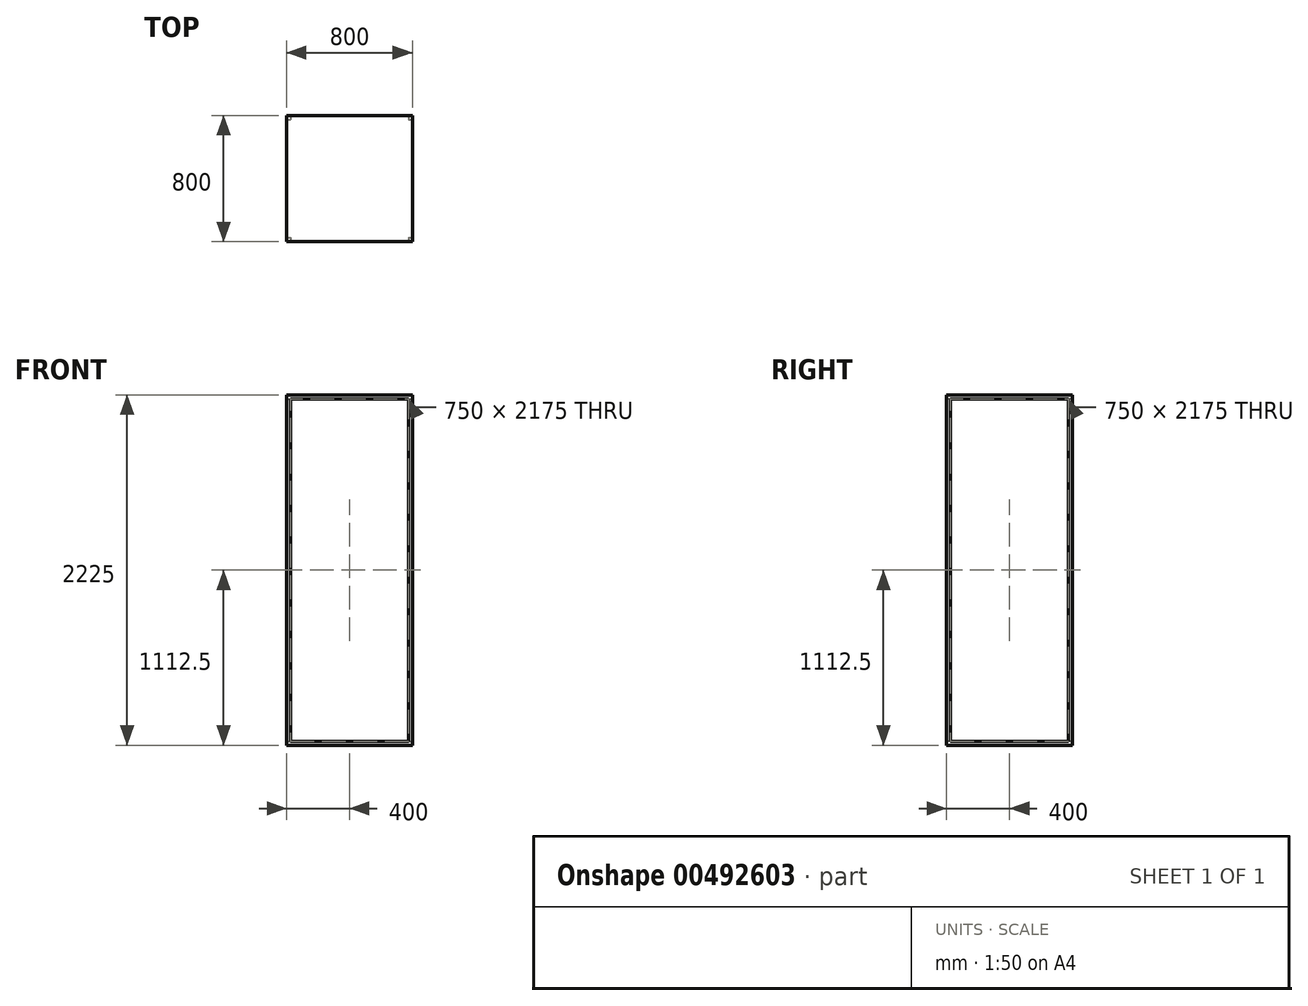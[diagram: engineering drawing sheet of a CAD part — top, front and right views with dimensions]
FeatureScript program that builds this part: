
annotation { "Feature Type Name" : "Feature", "Feature Type Description" : "" }
export const myFeature = defineFeature(function(context is Context, id is Id, definition is map)
    precondition{}
    {
        {
            var Q0;
            Q0=qCreatedBy(makeId("Front.planeOp"),FACE);
            var sketch = newSketch(context, id + "F0", { "sketchPlane" : qUnion([Q0])});
            skLineSegment(sketch, "E0.bottom", {"start": v(400, 1112.5) * mm, "end": v(-400, 1112.5) * mm});
            skLineSegment(sketch, "E0.top", {"start": v(400, -1112.5) * mm, "end": v(-400, -1112.5) * mm});
            skLineSegment(sketch, "E0.left", {"start": v(400, 1112.5) * mm, "end": v(400, -1112.5) * mm});
            skLineSegment(sketch, "E0.right", {"start": v(-400, 1112.5) * mm, "end": v(-400, -1112.5) * mm});
            skPoint(sketch, "E0.middle", {"position": v(0, 0) * mm});
            skSolve(sketch);
        }
        {
            var Q0;
            Q0=makeQuery(id+"F0.imprint","IMPRINT",FACE,{"disambiguationData":[TD([[makeQuery(id+"F0.imprint","IMPRINT",EDGE,{"derivedFrom":sQuery(id+"F0.wireOp",EDGE,"E0.bottom")}),1.0]])]});
            extrude(context, id + "F1", {"entities" : qUnion([Q0]), "depth" : 800 * mm});
        }
        {
            var Q0;
            Q0=makeQuery(id+"F1.opExtrude","CAP_FACE",FACE,{"disambiguationData":[OSD([sQuery(id+"F0.wireOp",EDGE,"E0.bottom"),sQuery(id+"F0.wireOp",EDGE,"E0.top"),sQuery(id+"F0.wireOp",EDGE,"E0.left"),sQuery(id+"F0.wireOp",EDGE,"E0.right")])],"isStart":false});
            var sketch = newSketch(context, id + "F2", { "sketchPlane" : qUnion([Q0])});
            skLineSegment(sketch, "E1.bottom", {"start": v(375, 1087.5) * mm, "end": v(-375, 1087.5) * mm});
            skLineSegment(sketch, "E1.top", {"start": v(375, -1087.5) * mm, "end": v(-375, -1087.5) * mm});
            skLineSegment(sketch, "E1.left", {"start": v(375, 1087.5) * mm, "end": v(375, -1087.5) * mm});
            skLineSegment(sketch, "E1.right", {"start": v(-375, 1087.5) * mm, "end": v(-375, -1087.5) * mm});
            skPoint(sketch, "E1.middle", {"position": v(0, 0) * mm});
            skSolve(sketch);
        }
        {
            var Q0;
            Q0=makeQuery(id+"F2.imprint","IMPRINT",FACE,{"disambiguationData":[TD([[makeQuery(id+"F2.imprint","IMPRINT",EDGE,{"derivedFrom":sQuery(id+"F2.wireOp",EDGE,"E1.bottom")}),1.0]])]});
            var Q1;
            Q1=makeQuery(id+"F1.opExtrude","CAP_FACE",FACE,{"disambiguationData":[OSD([sQuery(id+"F0.wireOp",EDGE,"E0.bottom"),sQuery(id+"F0.wireOp",EDGE,"E0.top"),sQuery(id+"F0.wireOp",EDGE,"E0.left"),sQuery(id+"F0.wireOp",EDGE,"E0.right")])],"isStart":true});
            extrude(context, id + "F3", {"entities" : qUnion([Q0]), "operationType" : NewBodyOperationType.REMOVE, "endBound" : BoundingType.UP_TO_SURFACE, "oppositeDirection" : true, "endBoundEntityFace" : qUnion([Q1]), "depth" : 25 * mm});
        }
        {
            var Q0;
            Q0=makeQuery(id+"F1.opExtrude","SWEPT_FACE",FACE,{"disambiguationData":[OSD([sQuery(id+"F0.wireOp",EDGE,"E0.left")])]});
            var sketch = newSketch(context, id + "F4", { "sketchPlane" : qUnion([Q0])});
            skLineSegment(sketch, "E2.bottom", {"start": v(-25, 1087.5) * mm, "end": v(-775, 1087.5) * mm});
            skLineSegment(sketch, "E2.top", {"start": v(-25, -1087.5) * mm, "end": v(-775, -1087.5) * mm});
            skLineSegment(sketch, "E2.left", {"start": v(-25, 1087.5) * mm, "end": v(-25, -1087.5) * mm});
            skLineSegment(sketch, "E2.right", {"start": v(-775, 1087.5) * mm, "end": v(-775, -1087.5) * mm});
            skPoint(sketch, "E2.middle", {"position": v(-400, 0) * mm});
            skPoint(sketch, "E2.middle.positionSnap0", {"position": v(-400, 1112.5) * mm});
            skPoint(sketch, "E2.centerSnap0", {"position": v(-400, 1112.5) * mm});
            skSolve(sketch);
        }
        {
            var Q0;
            Q0=makeQuery(id+"F4.imprint","IMPRINT",FACE,{"disambiguationData":[TD([[makeQuery(id+"F4.imprint","IMPRINT",EDGE,{"derivedFrom":sQuery(id+"F4.wireOp",EDGE,"E2.bottom")}),1.0]])]});
            var Q1;
            Q1=makeQuery(id+"F1.opExtrude","SWEPT_FACE",FACE,{"disambiguationData":[OSD([sQuery(id+"F0.wireOp",EDGE,"E0.right")])]});
            extrude(context, id + "F5", {"entities" : qUnion([Q0]), "operationType" : NewBodyOperationType.REMOVE, "endBound" : BoundingType.UP_TO_SURFACE, "oppositeDirection" : true, "endBoundEntityFace" : qUnion([Q1]), "depth" : 25 * mm});
        }
    });
